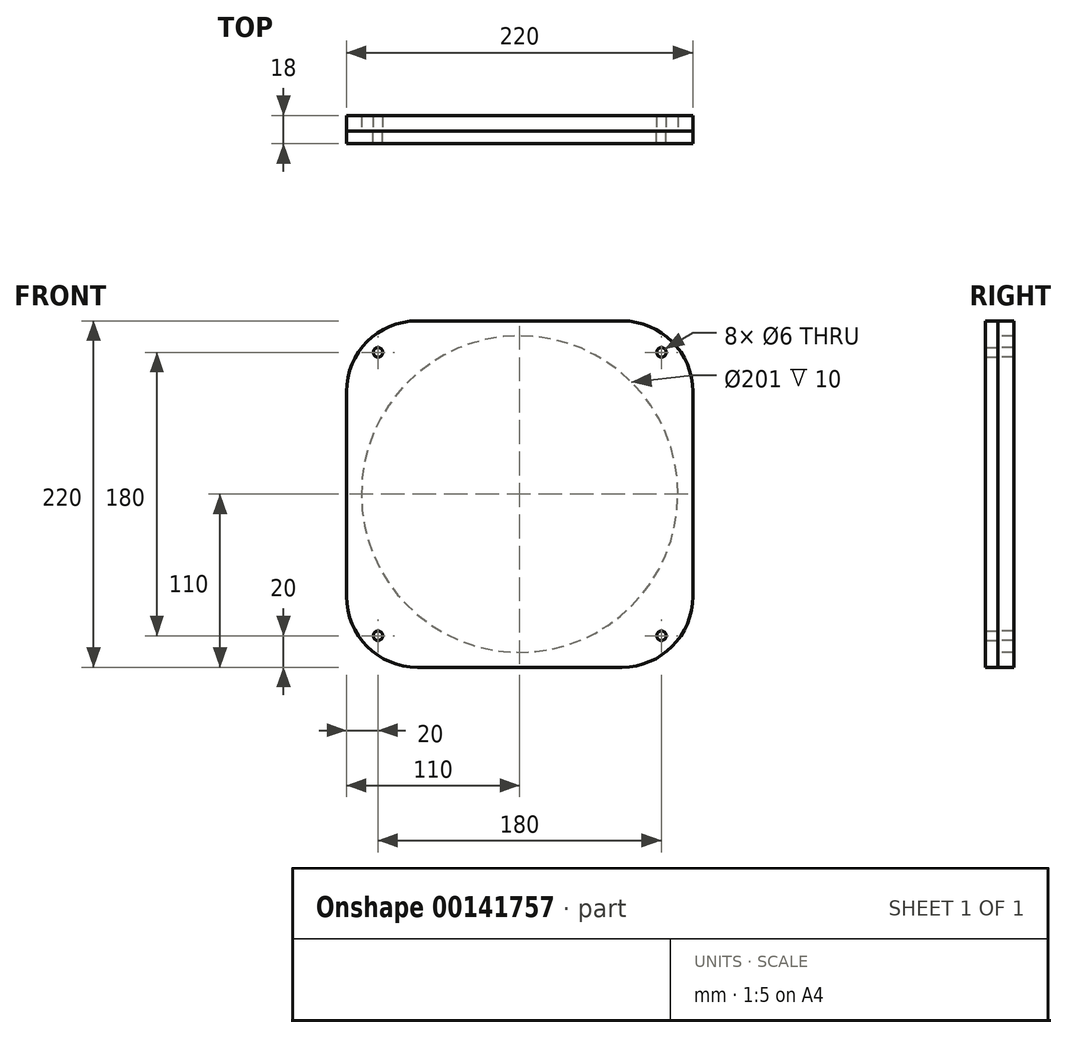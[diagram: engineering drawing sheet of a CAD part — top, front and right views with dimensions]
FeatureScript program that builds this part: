
annotation { "Feature Type Name" : "Feature", "Feature Type Description" : "" }
export const myFeature = defineFeature(function(context is Context, id is Id, definition is map)
    precondition{}
    {
        {
            var Q0;
            Q0=qCreatedBy(makeId("Front.planeOp"),FACE);
            var sketch = newSketch(context, id + "F0", { "sketchPlane" : qUnion([Q0])});
            skLineSegment(sketch, "E0.bottom", {"start": v(-65, 110) * mm, "end": v(65, 110) * mm});
            skLineSegment(sketch, "E0.top", {"start": v(-65, -110) * mm, "end": v(65, -110) * mm});
            skLineSegment(sketch, "E0.left", {"start": v(-110, 65) * mm, "end": v(-110, -65) * mm});
            skLineSegment(sketch, "E0.right", {"start": v(110, 65) * mm, "end": v(110, -65) * mm});
            skCircle(sketch, "E1", {"center": v(0, 0) * mm, "radius": 100.5 * mm});
            skPoint(sketch, "E2.visualSharp", {"position": v(-110, 110) * mm});
            skArc(sketch, "E2.filletArc", {"start": v(-65, 110) * mm, "mid": v(-96.82, 96.82) * mm, "end": v(-110, 65) * mm});
            skPoint(sketch, "E3.visualSharp", {"position": v(110, 110) * mm});
            skArc(sketch, "E3.filletArc", {"start": v(110, 65) * mm, "mid": v(96.82, 96.82) * mm, "end": v(65, 110) * mm});
            skPoint(sketch, "E4.visualSharp", {"position": v(110, -110) * mm});
            skArc(sketch, "E4.filletArc", {"start": v(65, -110) * mm, "mid": v(96.82, -96.82) * mm, "end": v(110, -65) * mm});
            skPoint(sketch, "E5.visualSharp", {"position": v(-110, -110) * mm});
            skArc(sketch, "E5.filletArc", {"start": v(-110, -65) * mm, "mid": v(-96.82, -96.82) * mm, "end": v(-65, -110) * mm});
            skLineSegment(sketch, "E6", {"start": v(-90, 90) * mm, "end": v(90, 90) * mm, "construction": true});
            skLineSegment(sketch, "E7", {"start": v(90, 90) * mm, "end": v(90, -90) * mm, "construction": true});
            skLineSegment(sketch, "E8", {"start": v(-90, 90) * mm, "end": v(-90, -90) * mm, "construction": true});
            skLineSegment(sketch, "E9", {"start": v(-90, -90) * mm, "end": v(90, -90) * mm, "construction": true});
            skCircle(sketch, "E10", {"center": v(-90, 90) * mm, "radius": 3 * mm});
            skCircle(sketch, "E11", {"center": v(90, 90) * mm, "radius": 3 * mm});
            skCircle(sketch, "E12", {"center": v(90, -90) * mm, "radius": 3 * mm});
            skCircle(sketch, "E13", {"center": v(-90, -90) * mm, "radius": 3 * mm});
            skSolve(sketch);
        }
        {
            var Q0;
            Q0=makeQuery(id+"F0.imprint","IMPRINT",FACE,{"disambiguationData":[TD([[makeQuery(id+"F0.imprint","IMPRINT",EDGE,{"derivedFrom":sQuery(id+"F0.wireOp",EDGE,"E0.bottom")}),-1.0]])]});
            extrude(context, id + "F1", {"entities" : qUnion([Q0]), "oppositeDirection" : true, "depth" : 10 * mm});
        }
        {
            var Q0;
            Q0=makeQuery(id+"F0.imprint","IMPRINT",FACE,{"disambiguationData":[TD([[makeQuery(id+"F0.imprint","IMPRINT",EDGE,{"derivedFrom":sQuery(id+"F0.wireOp",EDGE,"E0.bottom")}),-1.0]])]});
            var Q1;
            Q1=makeQuery(id+"F0.imprint","IMPRINT",FACE,{"disambiguationData":[TD([[makeQuery(id+"F0.imprint","IMPRINT",EDGE,{"derivedFrom":sQuery(id+"F0.wireOp",EDGE,"E1")}),1.0]])]});
            extrude(context, id + "F2", {"entities" : qUnion([Q0, Q1]), "depth" : 8 * mm});
        }
    });
